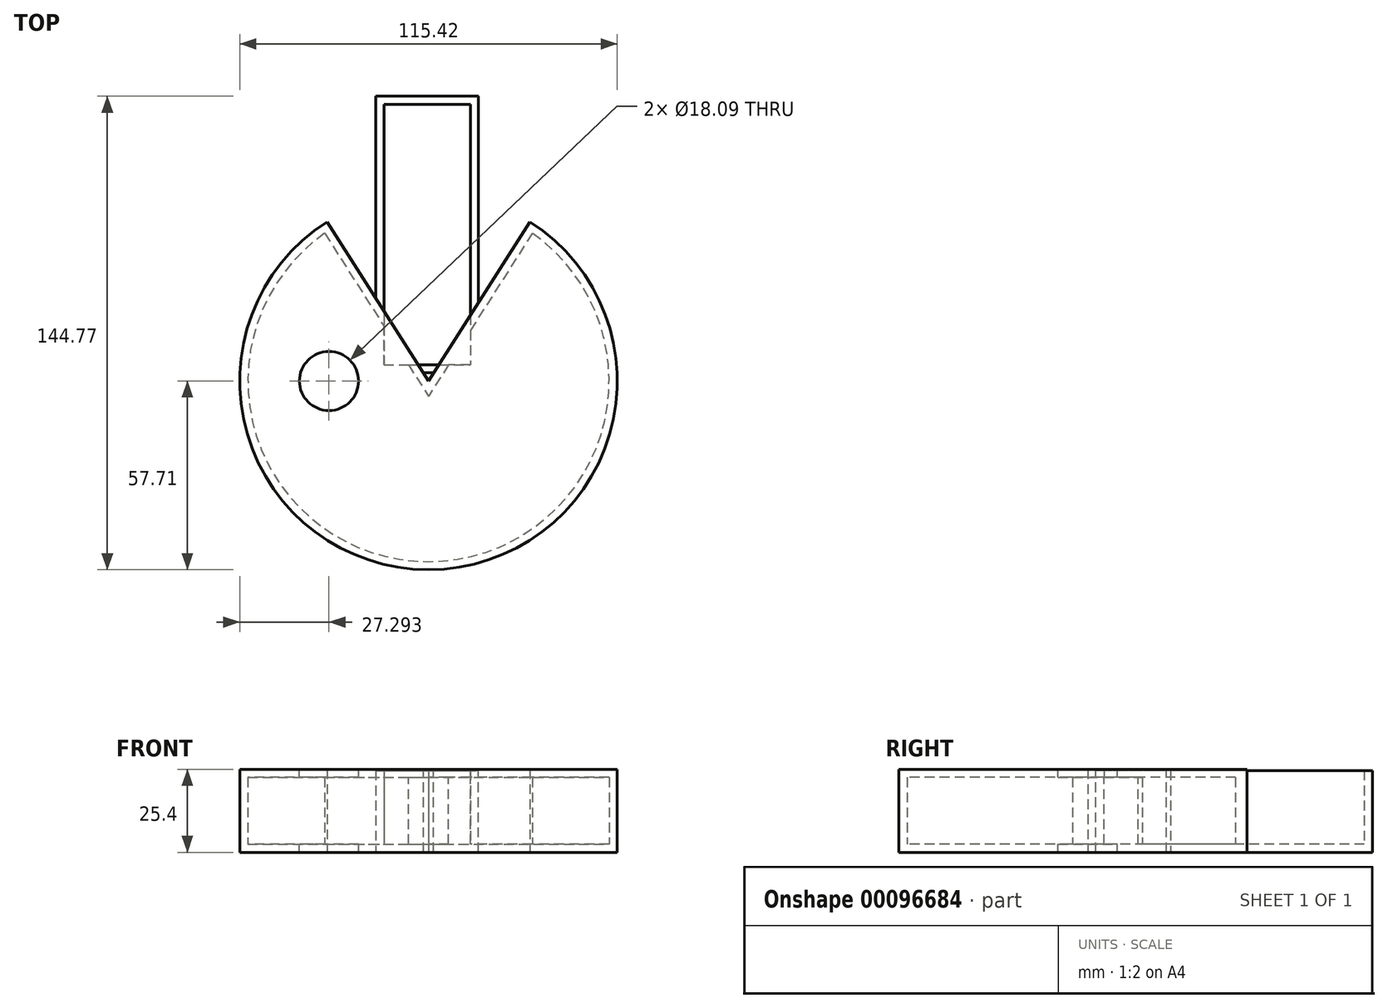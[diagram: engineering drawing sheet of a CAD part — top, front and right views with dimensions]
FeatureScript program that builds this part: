
annotation { "Feature Type Name" : "Feature", "Feature Type Description" : "" }
export const myFeature = defineFeature(function(context is Context, id is Id, definition is map)
    precondition{}
    {
        {
            var Q0;
            Q0=qCreatedBy(makeId("Top.planeOp"),FACE);
            var sketch = newSketch(context, id + "F0", { "sketchPlane" : qUnion([Q0])});
            skArc(sketch, "E0", {"start": v(-31, 48.67) * mm, "mid": v(-55.4, -16.15) * mm, "end": v(0, -57.71) * mm});
            skLineSegment(sketch, "E1", {"start": v(-31, 48.67) * mm, "end": v(0, 0) * mm});
            skLineSegment(sketch, "E2.MirrorCS", {"start": v(31, 48.67) * mm, "end": v(0, 0) * mm});
            skArc(sketch, "E3.MirrorCS", {"start": v(31, 48.67) * mm, "mid": v(55.4, -16.15) * mm, "end": v(0, -57.71) * mm});
            skArc(sketch, "E4.0", {"start": v(-36.38, 57.1) * mm, "mid": v(-65, -18.95) * mm, "end": v(0, -67.71) * mm});
            skLineSegment(sketch, "E5.0", {"start": v(38.28, 44.04) * mm, "end": v(37.93, 43.5) * mm});
            skSolve(sketch);
        }
        {
            var Q0;
            Q0=makeQuery(id+"F0.imprint","IMPRINT",FACE,{"disambiguationData":[TD([[makeQuery(id+"F0.imprint","IMPRINT",EDGE,{"derivedFrom":sQuery(id+"F0.wireOp",EDGE,"HaEsUCMS-q9Fc-bmMJ-bskc-LkfczHZ6eroA")}),1.0]])]});
            var Q1;
            Q1=makeQuery(id+"F0.imprint","IMPRINT",FACE,{"disambiguationData":[TD([[makeQuery(id+"F0.imprint","IMPRINT",EDGE,{"derivedFrom":sQuery(id+"F0.wireOp",EDGE,"E0")}),1.0]])]});
            extrude(context, id + "F1", {"entities" : qUnion([Q0, Q1]), "depth" : 25.4 * mm});
        }
        {
            var Q0;
            Q0=makeQuery(id+"F1.opExtrude","SWEPT_FACE",FACE,{"disambiguationData":[OSD([sQuery(id+"F0.wireOp",EDGE,"E1")])]});
            var sketch = newSketch(context, id + "F2", { "sketchPlane" : qUnion([Q0])});
            skSolve(sketch);
        }
        {
            var Q0;
            Q0=makeQuery(id+"F1.opExtrude","CAP_FACE",FACE,{"disambiguationData":[OSD([sQuery(id+"F0.wireOp",EDGE,"E0"),sQuery(id+"F0.wireOp",EDGE,"E1"),sQuery(id+"F0.wireOp",EDGE,"E2.MirrorCS"),sQuery(id+"F0.wireOp",EDGE,"E3.MirrorCS")])],"isStart":false});
            var sketch = newSketch(context, id + "F3", { "sketchPlane" : qUnion([Q0])});
            skArc(sketch, "E6", {"start": v(-37.14, 6.04) * mm, "mid": v(-29.41, -8.99) * mm, "end": v(-25.19, 7.38) * mm});
            skArc(sketch, "E7", {"start": v(-25.19, 7.38) * mm, "mid": v(-31.42, 8.99) * mm, "end": v(-37.14, 6.04) * mm});
            skSolve(sketch);
        }
        {
            var Q0;
            Q0=qCreatedBy(makeId("Top.planeOp"),FACE);
            var sketch = newSketch(context, id + "F4", { "sketchPlane" : qUnion([Q0])});
            skLineSegment(sketch, "E8.bottom", {"start": v(-16.12, 87.06) * mm, "end": v(15.28, 87.06) * mm});
            skLineSegment(sketch, "E8.top", {"start": v(-16.12, 2.47) * mm, "end": v(15.28, 2.47) * mm});
            skLineSegment(sketch, "E8.left", {"start": v(-16.12, 87.06) * mm, "end": v(-16.12, 2.47) * mm});
            skLineSegment(sketch, "E8.right", {"start": v(15.28, 87.06) * mm, "end": v(15.28, 2.47) * mm});
            skSolve(sketch);
        }
        {
            var Q0;
            Q0 = qSketchRegion(id + "F4", true);
            extrude(context, id + "F5", {"entities" : qUnion([Q0]), "operationType" : NewBodyOperationType.ADD, "depth" : 25 * mm});
        }
        {
            var Q0;
            Q0=makeQuery(id+"F5.opExtrude","CAP_FACE",FACE,{"disambiguationData":[OSD([sQuery(id+"F4.wireOp",EDGE,"E8.bottom"),sQuery(id+"F4.wireOp",EDGE,"E8.top"),sQuery(id+"F4.wireOp",EDGE,"E8.left"),sQuery(id+"F4.wireOp",EDGE,"E8.right")])],"isStart":false});
            shell(context, id + "F6", {"entities" : qUnion([Q0]), "thickness" : 2.5 * mm});
        }
        {
            var Q0;
            Q0 = qSketchRegion(id + "F3", true);
            extrude(context, id + "F7", {"entities" : qUnion([Q0]), "operationType" : NewBodyOperationType.REMOVE, "oppositeDirection" : true, "depth" : 50 * mm});
        }
    });
